# Revit family: MCE Combined Series
name_source: partatom
category: Mechanical Equipment
revit_build: Autodesk Revit 2018 (Build: 20170223_1515(x64)
units: mm (PartAtom-declared; Revit-internal decimal feet)

## family parameters
Always vertical = Yes
Cut with Voids When Loaded = No
OmniClass Number = 23.75.00.00
OmniClass Title = Climate Control (HVAC)
Part Type = Normal
Room Calculation Point = No
Round Connector Dimension = Use Diameter
Shared = No
Work Plane-Based = No

## types (19) — shared parameters
R0 Central = Yes
R1 Central = Yes
R2 Central = Yes
R3 Central = Yes

## per-type parameters (varying)
| type | A | B | C | E - Box 2 | E-box 2 | E-connector height | Electric Heater Power in KW (each) | Electrical Connector Offset A | Electrical Connector Offset B | Fan Power in KW (each) | No. of Electric Heaters | No. of Fans | Pump Flow (l/s) | Pump Power (KW) | R0 height | R1 height | R2 height | R3 height | Ref Offset c-c | Ref Pipe Offset A | Specify Type | Weight (Empty) | Weight (In operation) |
| MCE A4-17 | 1870 mm  [stored 6.13517 ft] | 1030 mm | 3400 mm | DISABLED | No | 2920 mm | 2 | 1032 mm | 257 mm  [stored 0.843176 ft] | 2.2 | 1 | 2 | 3,1 | 0,55 | 1005 mm  [stored 3.29724 ft] | 1620 mm | 1920 mm | 2330 mm | 914 mm | 1110 mm  [stored 3.64173 ft] | MCE A : MCC-MCE A4-17.CVCS.R01 | 1130-1500 | 2530-2700 |
| MCE B4-17 | 2770 mm | 1030 mm | 3400 mm | DISABLED | No | 2920 mm | 3 | 1482 mm | 257 mm  [stored 0.843176 ft] | 2.2 | 1 | 3 | 4,9 | 0,55 | 1005 mm  [stored 3.29724 ft] | 1620 mm | 1920 mm | 2330 mm | 914 mm | 1560 mm | MCE B : MCC-MCE B4-17.CVCS.R01 | 1530-2070 | 3200-3820 |
| MCE D4-17 | 2850 mm | 1235 mm | 3480 mm | DISABLED | No | 2920 mm | 3 | 1522 mm | 360 mm | 4 | 1 | 2 | 6 | 0.75 | 1005 mm  [stored 3.29724 ft] | 1620 mm | 1920 mm | 2330 mm | 914 mm | 1600 mm  [stored 5.24934 ft] | MCE D : MCC-MCE D4-17.CVCS.R01 | 1680-2380 | 3700-4400 |
| MCE A-17 | 1870 mm  [stored 6.13517 ft] | 1030 mm | 3160 mm | DISABLED | No | 2670 mm | 2 | 1032 mm | 257 mm  [stored 0.843176 ft] | 1.5 | 1 | 2 | 3,1 | 0,55 | 1005 mm  [stored 3.29724 ft] | 1615 mm | 1850 mm  [stored 6.06955 ft] | 2090 mm | 914 mm | 1110 mm  [stored 3.64173 ft] | MCE A : MCC-MCE A-17.CVCS.R01 | 1130-1500 | 2530-2700 |
| MCE B-17 | 2770 mm | 1030 mm | 3160 mm | DISABLED | No | 2670 mm | 3 | 1482 mm | 257 mm  [stored 0.843176 ft] | 1,5 | 1 | 3 | 4,9 | 0,55 | 1005 mm  [stored 3.29724 ft] | 1615 mm | 1850 mm  [stored 6.06955 ft] | 2090 mm | 914 mm | 1560 mm | MCE B : MCC-MCE B-17.CVCS.R01 | 1530-2070 | 3200-3820 |
| MCE D-17 | 2850 mm | 1235 mm | 3250 mm | DISABLED | No | 2700 mm | 3 | 1522 mm | 360 mm | 3 | 1 | 2 | 6 | 0.75 | 1035 mm  [stored 3.39567 ft] | 1645 mm | 1880 mm | 2120 mm | 914 mm | 1600 mm  [stored 5.24934 ft] | MCE D : MCC-MCE D-17.CVCS.R01 | 1680-2380 | 3700-4400 |
| MCE E-17 | 3670 mm | 1235 mm | 3250 mm | DISABLED | No | 2700 mm | 4.5 | 1932 mm  [stored 6.33858 ft] | 360 mm | 3 | 1 | 3 | 7,8 | 1,1 | 1035 mm  [stored 3.39567 ft] | 1645 mm | 1880 mm | 2120 mm | 2719 mm | 2010 mm  [stored 6.59449 ft] | MCE E : MCC-MCE E-17.CVCS.R01 | 2030-2840 | 4680-5570 |
| MCE H-17 | 3670 mm | 1505 mm  [stored 4.93766 ft] | 3460 mm | DISABLED | Yes | 2900 mm | 4.5 | 1932 mm  [stored 6.33858 ft] | 495 mm | 3 | 1 | 3 | 9.6 | 1.1 | 1235 mm | 1845 mm | 2080 mm | 2320 mm | 914 mm | 2010 mm  [stored 6.59449 ft] | MCE H : MCC-MCE H-17.CVCS.R01 | 2450-3440 | 5460-6600 |
| MCE N-19 | 3620 mm | 2360 mm | 3650 mm | DISABLED | No | 2960 mm | 7.5 | 1907 mm | 922 mm | 15 | 1 | 1 | 15,4 | 2,2 | 1325 mm | 1935 mm | 2170 mm | 2410 mm | 1130 mm  [stored 3.70735 ft] | 1985 mm | MCE N : MCC-MCE N-19.CVCS.R01 | 3770-4820 | 8050-9660 |
| MCE P-17 | 4570 mm | 2360 mm | 3800 mm | DISABLED | No | 3110 mm | 5 | 2382 mm | 922 mm | 7,5 | 2 | 2 | 19,3 | 3,0 | 1325 mm | 2010 mm  [stored 6.59449 ft] | 2275 mm | 2540 mm | 1130 mm  [stored 3.70735 ft] | 2460 mm | MCE P : MCC-MCE P-17.CVCS.R01 | 4140-5980 | 9900-11900 |
| MCE Q-17 | 5500 mm | 2360 mm | 3800 mm | DISABLED | No | 3110 mm | 7,5 | 2847 mm | 922 mm | 11 | 2 | 2 | 23,2 | 4,0 | 1325 mm | 2010 mm  [stored 6.59449 ft] | 2275 mm | 2540 mm | 1130 mm  [stored 3.70735 ft] | 2925 mm | MCE Q : MCC-MCE Q-17.CVCS.R01 | 4890-7180 | 11030-13500 |
| MCE S-17 | 5470 mm | 2960 mm | 4285 mm | DISABLED | No | 3520 mm | 7,5 | 2832 mm | 1222 mm | 11 | 2 | 2 | 29,4 | 4,0 | 1635 mm | 2320 mm | 2585 mm | 2850 mm | 1130 mm  [stored 3.70735 ft] | 2910 mm | MCE S : MCC-MCE S-17.CVCS.R01 | 5830-8470 | 14070-17080 |
| MCE E4-17 | 3670 mm | 1235 mm | 3480 mm | DISABLED | No | 2950 mm | 4.5 | 1932 mm  [stored 6.33858 ft] | 360 mm | 3 | 1 | 3 | 7,8 | 1,1 | 1035 mm  [stored 3.39567 ft] | 1620 mm | 1920 mm | 2360 mm | 914 mm | 2010 mm  [stored 6.59449 ft] | MCE E : MCC-MCE E4-17.CVCS.R01 | 2030-2840 | 4680-5570 |
| MCE H4-17 | 3670 mm | 1505 mm  [stored 4.93766 ft] | 3700 mm | DISABLED | No | 3150 mm | 4.5 | 1932 mm  [stored 6.33858 ft] | 495 mm | 4 | 1 | 3 | 9.6 | 1.1 | 1235 mm | 1620 mm | 1920 mm | 2560 mm | 914 mm | 2010 mm  [stored 6.59449 ft] | MCE H : MCC-MCE H4-17.CVCS.R01 | 2450-3440 | 5460-6600 |
| MCE N4-19 | 3620 mm | 2360 mm | 3890 mm | DISABLED | No | 3210 mm | 7.5 | 1907 mm | 922 mm | 15 | 1 | 1 | 15,4 | 2,2 | 1325 mm | 1620 mm | 1920 mm | 2650 mm | 1130 mm  [stored 3.70735 ft] | 1985 mm | MCE N : MCC-MCE N4-19.CVCS.R01 | 3770-4820 | 8050-9660 |
| MCE P4-17 | 4570 mm | 2360 mm | 4030 mm | DISABLED | No | 3240 mm | 5 | 2382 mm | 922 mm | 11 | 2 | 2 | 19,3 | 3,0 | 1325 mm | 1620 mm | 1920 mm | 2805 mm | 1130 mm  [stored 3.70735 ft] | 2460 mm | MCE P : MCC-MCE P4-17.CVCS.R01 | 4140-5980 | 9900-11900 |
| MCE Q4-17 | 5500 mm | 2360 mm | 4030 mm | DISABLED | No | 3340 mm | 7,5 | 2847 mm | 922 mm | 11 | 2 | 2 | 23,2 | 4,0 | 1325 mm | 1620 mm | 1920 mm | 2805 mm | 1130 mm  [stored 3.70735 ft] | 2925 mm | MCE Q : MCC-MCE Q4-17.CVCS.R01 | 4890-7180 | 11030-13500 |
| MCE S4-17 | 5470 mm | 2960 mm | 4560 mm | DISABLED | No | 3785 mm | 7,5 | 2832 mm | 1222 mm | 15 | 2 | 2 | 29,4 | 4,0 | 1635 mm | 2300 mm | 2500 mm | 3115 mm | 1130 mm  [stored 3.70735 ft] | 2910 mm | MCE S : MCC-MCE S4-17.CVCS.R01 | 5830-8470 | 14070-17080 |
| MCE T-17 | 5782 mm | 3600 mm | 4430 mm | ENABLED | Yes | 3397 mm | 7,5 | 2988 mm | 1542 mm | 15 | 2 | 2 | 2 x 20,1 | 2 x 4,0 | 1607 mm | 1800 mm  [stored 5.90551 ft] | 2557 mm | 2822 mm | 1787 mm  [stored 5.86286 ft] | 3066 mm | MCE T : MCC-MCE T-17.CVCS.R02 | 10600-11400 | 16100-17230 |

note: [stored X ft] marks values corroborated as IEEE doubles in the binary element streams (Revit-internal decimal feet)

## geometry (parser evidence)
native form markers: Sweep x93
no freeform markers — native parametric forms only
